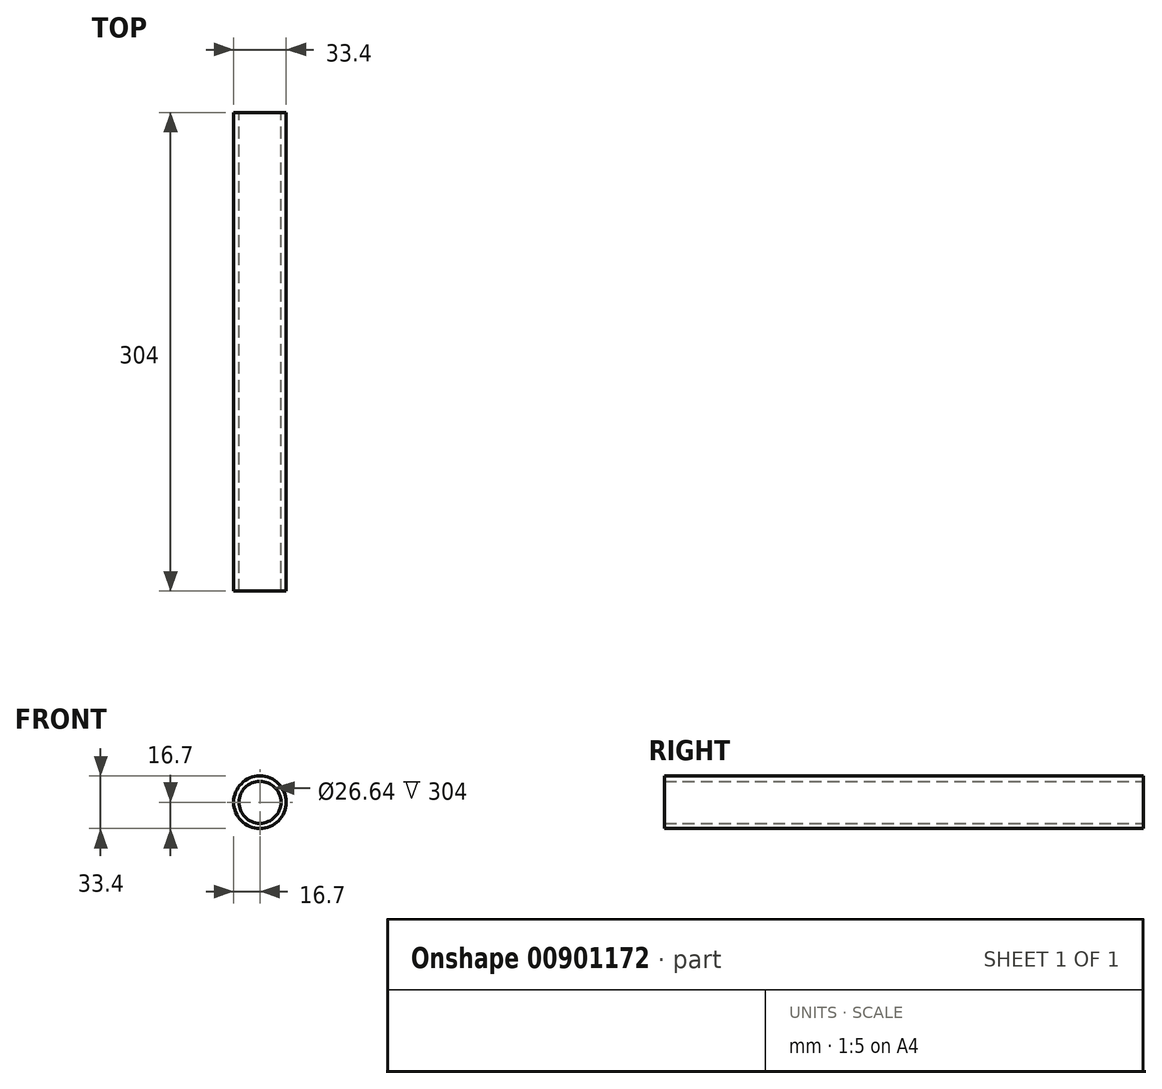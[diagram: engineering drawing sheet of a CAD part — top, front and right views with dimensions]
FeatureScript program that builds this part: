
annotation { "Feature Type Name" : "Feature", "Feature Type Description" : "" }
export const myFeature = defineFeature(function(context is Context, id is Id, definition is map)
    precondition{}
    {
        {
            var Q0;
            Q0=qCreatedBy(makeId("Front.planeOp"),FACE);
            var sketch = newSketch(context, id + "F0", { "sketchPlane" : qUnion([Q0])});
            skCircle(sketch, "E0", {"center": v(0, 0) * mm, "radius": 16.7 * mm});
            skCircle(sketch, "E1", {"center": v(0, 0) * mm, "radius": 13.32 * mm});
            skSolve(sketch);
        }
        {
            var Q0;
            Q0=makeQuery(id+"F0.imprint","IMPRINT",FACE,{"disambiguationData":[TD([[makeQuery(id+"F0.imprint","IMPRINT",EDGE,{"derivedFrom":sQuery(id+"F0.wireOp",EDGE,"E0")}),1.0]])]});
            extrude(context, id + "F1", {"entities" : qUnion([Q0]), "depth" : 304 * mm, "offsetDistance" : 25.4 * mm});
        }
    });
